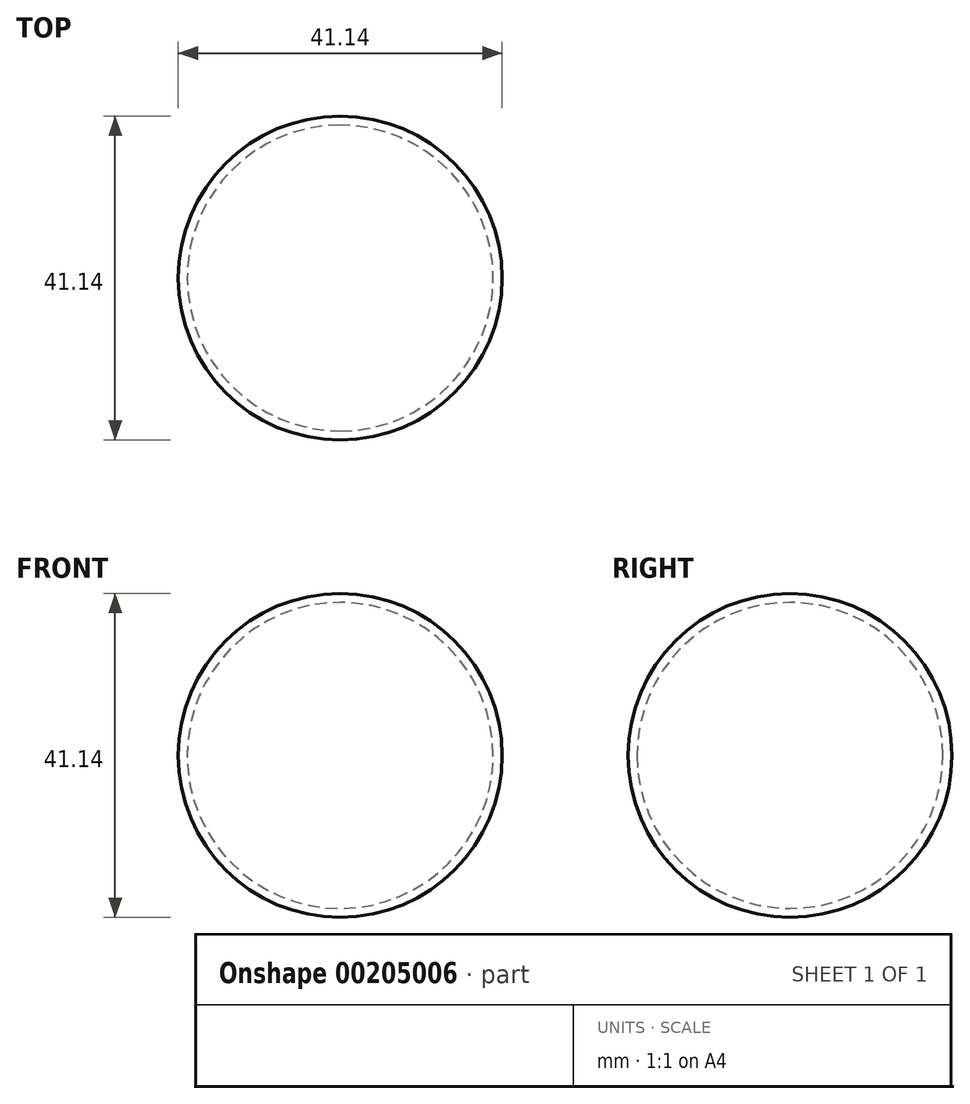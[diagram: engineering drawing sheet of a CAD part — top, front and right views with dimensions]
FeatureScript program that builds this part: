
annotation { "Feature Type Name" : "Feature", "Feature Type Description" : "" }
export const myFeature = defineFeature(function(context is Context, id is Id, definition is map)
    precondition{}
    {
        {
            var Q0;
            Q0=qCreatedBy(makeId("Top.planeOp"),FACE);
            var sketch = newSketch(context, id + "F0", { "sketchPlane" : qUnion([Q0])});
            skCircle(sketch, "E0", {"center": v(0, 0) * mm, "radius": 20.57 * mm});
            skCircle(sketch, "E1", {"center": v(0, 0) * mm, "radius": 19.43 * mm});
            skLineSegment(sketch, "E2", {"start": v(0, 0) * mm, "end": v(0, 20.57) * mm});
            skLineSegment(sketch, "E3", {"start": v(0, 20.57) * mm, "end": v(0, -20.57) * mm});
            skSolve(sketch);
        }
        {
            var Q0;
            {var subQ0=sQuery(id+"F0.wireOp",EDGE,"E3");var subQ1=sQuery(id+"F0.wireOp",EDGE,"E0");var subQ2=makeQuery(id+"F0.imprint","INTERSECT",VERTEX,{"disambiguationData":[OD(0.0)],"derivedFrom":[subQ1,subQ0]});Q0=makeQuery(id+"F0.imprint","IMPRINT",FACE,{"disambiguationData":[TD([[makeQuery(id+"F0.imprint","IMPRINT",EDGE,{"disambiguationData":[TD([[subQ2,1.0]])],"derivedFrom":subQ1}),1.0]])]});}
            var Q1;
            Q1=sQuery(id+"F0.wireOp",EDGE,"E3");
            revolve(context, id + "F1", {"entities" : qUnion([Q0]), "axis" : qUnion([Q1]), "revolveType" : RevolveType.FULL});
        }
    });
